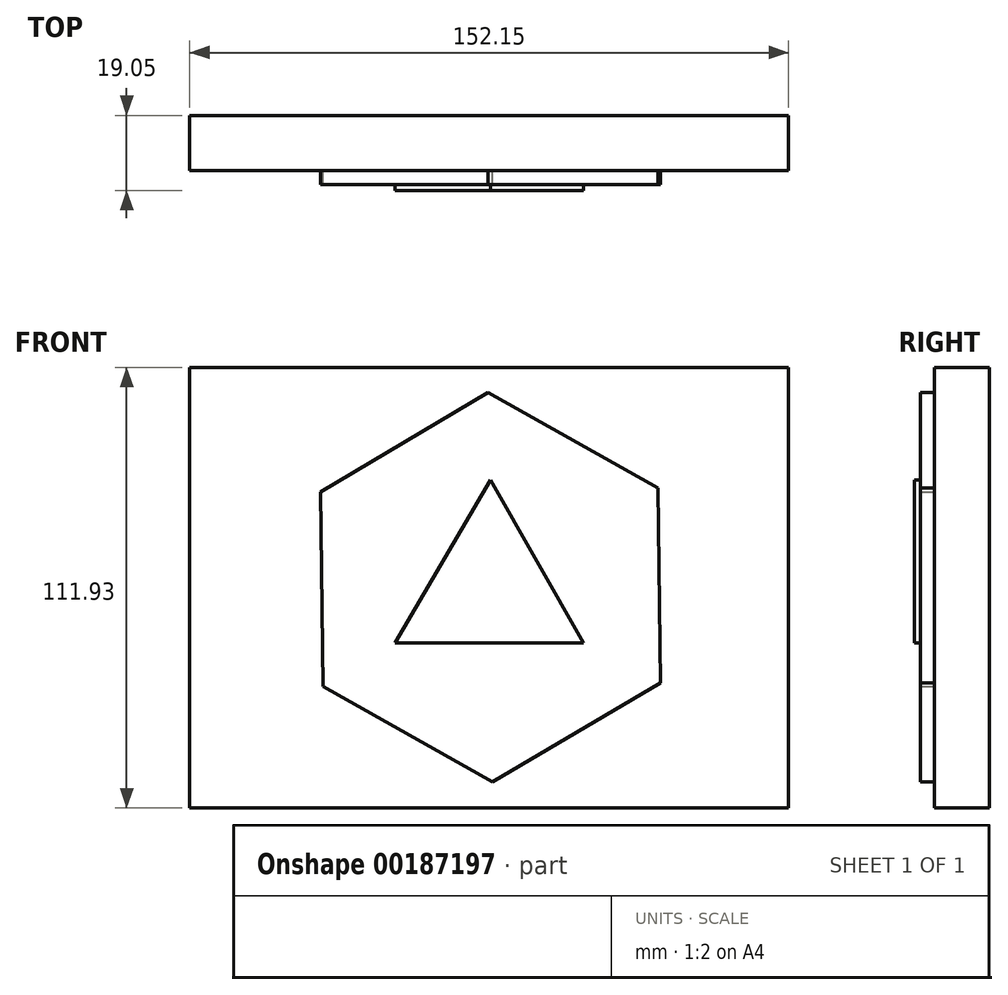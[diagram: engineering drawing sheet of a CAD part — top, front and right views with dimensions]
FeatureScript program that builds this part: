
annotation { "Feature Type Name" : "Feature", "Feature Type Description" : "" }
export const myFeature = defineFeature(function(context is Context, id is Id, definition is map)
    precondition{}
    {
        {
            var Q0;
            Q0=qCreatedBy(makeId("Front.planeOp"),FACE);
            var sketch = newSketch(context, id + "F0", { "sketchPlane" : qUnion([Q0])});
            skLineSegment(sketch, "E0.bottom", {"start": v(-76.37, 55.82) * mm, "end": v(75.78, 55.82) * mm});
            skLineSegment(sketch, "E0.top", {"start": v(-76.37, -56.1) * mm, "end": v(75.78, -56.1) * mm});
            skLineSegment(sketch, "E0.left", {"start": v(-76.37, 55.82) * mm, "end": v(-76.37, -56.1) * mm});
            skLineSegment(sketch, "E0.right", {"start": v(75.78, 55.82) * mm, "end": v(75.78, -56.1) * mm});
            skSolve(sketch);
        }
        {
            var Q0;
            Q0=makeQuery(id+"F0.imprint","IMPRINT",FACE,{"disambiguationData":[TD([[makeQuery(id+"F0.imprint","IMPRINT",EDGE,{"derivedFrom":sQuery(id+"F0.wireOp",EDGE,"E0.bottom")}),-1.0]])]});
            extrude(context, id + "F1", {"entities" : qUnion([Q0]), "depth" : 13.97 * mm});
        }
        {
            var Q0;
            Q0=makeQuery(id+"F1.opExtrude","CAP_FACE",FACE,{"disambiguationData":[OSD([sQuery(id+"F0.wireOp",EDGE,"E0.bottom"),sQuery(id+"F0.wireOp",EDGE,"E0.top"),sQuery(id+"F0.wireOp",EDGE,"E0.left"),sQuery(id+"F0.wireOp",EDGE,"E0.right")])],"isStart":false});
            var sketch = newSketch(context, id + "F2", { "sketchPlane" : qUnion([Q0])});
            skCircle(sketch, "E1.cCircle", {"center": v(0, 0) * mm, "radius": 42.86 * mm, "construction": true});
            skLineSegment(sketch, "E1.0", {"start": v(-43.15, 24.25) * mm, "end": v(-0.57, 49.5) * mm});
            skLineSegment(sketch, "E1.1", {"start": v(-0.57, 49.5) * mm, "end": v(42.58, 25.24) * mm});
            skLineSegment(sketch, "E1.2", {"start": v(42.58, 25.24) * mm, "end": v(43.15, -24.25) * mm});
            skLineSegment(sketch, "E1.3", {"start": v(43.15, -24.25) * mm, "end": v(0.57, -49.5) * mm});
            skLineSegment(sketch, "E1.4", {"start": v(0.57, -49.5) * mm, "end": v(-42.58, -25.24) * mm});
            skLineSegment(sketch, "E1.5", {"start": v(-42.58, -25.24) * mm, "end": v(-43.15, 24.25) * mm});
            skPoint(sketch, "E1.0.midPoint", {"position": v(-21.86, 36.87) * mm});
            skSolve(sketch);
        }
        {
            var Q0;
            Q0=makeQuery(id+"F2.imprint","IMPRINT",FACE,{"disambiguationData":[TD([[makeQuery(id+"F2.imprint","IMPRINT",EDGE,{"derivedFrom":sQuery(id+"F2.wireOp",EDGE,"E1.0")}),-1.0]])]});
            extrude(context, id + "F3", {"entities" : qUnion([Q0]), "operationType" : NewBodyOperationType.ADD, "depth" : 3.56 * mm});
        }
        {
            var Q0;
            Q0=makeQuery(id+"F3.opExtrude","CAP_FACE",FACE,{"disambiguationData":[OSD([sQuery(id+"F2.wireOp",EDGE,"E1.0"),sQuery(id+"F2.wireOp",EDGE,"E1.1"),sQuery(id+"F2.wireOp",EDGE,"E1.2"),sQuery(id+"F2.wireOp",EDGE,"E1.3"),sQuery(id+"F2.wireOp",EDGE,"E1.4"),sQuery(id+"F2.wireOp",EDGE,"E1.5")])],"isStart":false});
            var sketch = newSketch(context, id + "F4", { "sketchPlane" : qUnion([Q0])});
            skLineSegment(sketch, "E2", {"start": v(0, 27.25) * mm, "end": v(-24.2, -14.14) * mm});
            skLineSegment(sketch, "E3", {"start": v(-24.2, -14.14) * mm, "end": v(23.6, -14.14) * mm});
            skLineSegment(sketch, "E4", {"start": v(0, 27.25) * mm, "end": v(23.6, -14.14) * mm});
            skSolve(sketch);
        }
        {
            var Q0;
            Q0=makeQuery(id+"F4.imprint","IMPRINT",FACE,{"disambiguationData":[TD([[makeQuery(id+"F4.imprint","IMPRINT",EDGE,{"derivedFrom":sQuery(id+"F4.wireOp",EDGE,"E2")}),1.0]])]});
            extrude(context, id + "F5", {"entities" : qUnion([Q0]), "operationType" : NewBodyOperationType.ADD, "depth" : 1.52 * mm});
        }
    });
